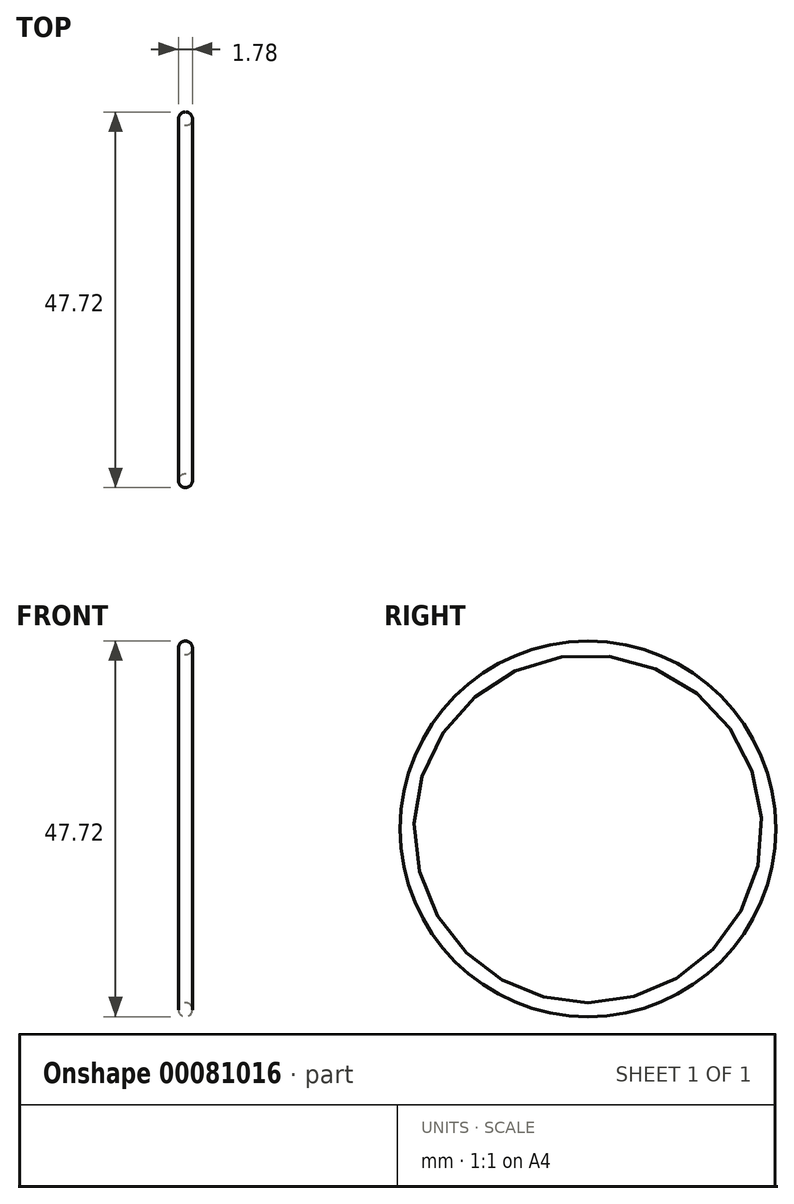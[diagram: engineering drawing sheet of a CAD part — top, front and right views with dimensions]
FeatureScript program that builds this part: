
annotation { "Feature Type Name" : "Feature", "Feature Type Description" : "" }
export const myFeature = defineFeature(function(context is Context, id is Id, definition is map)
    precondition{}
    {
        {
            var Q0;
            Q0=qCreatedBy(makeId("Front.planeOp"),FACE);
            var sketch = newSketch(context, id + "F0", { "sketchPlane" : qUnion([Q0])});
            skLineSegment(sketch, "E0", {"start": v(0, 0) * mm, "end": v(-6.06, 0) * mm, "construction": true});
            skCircle(sketch, "E1", {"center": v(0, 22.97) * mm, "radius": 0.89 * mm});
            skSolve(sketch);
        }
        {
            var Q0;
            Q0=makeQuery(id+"F0.imprint","IMPRINT",FACE,{"disambiguationData":[TD([[makeQuery(id+"F0.imprint","IMPRINT",EDGE,{"derivedFrom":sQuery(id+"F0.wireOp",EDGE,"E1")}),1.0]])]});
            var Q1;
            Q1=sQuery(id+"F0.wireOp",EDGE,"E0");
            revolve(context, id + "F1", {"entities" : qUnion([Q0]), "axis" : qUnion([Q1]), "revolveType" : RevolveType.FULL});
        }
    });
